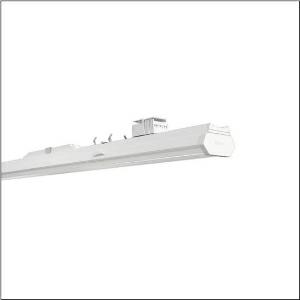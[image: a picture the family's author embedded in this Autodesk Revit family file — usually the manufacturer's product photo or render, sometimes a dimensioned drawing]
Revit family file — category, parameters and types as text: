
# Revit family: licross_11_protected_mo_51td12dn495g
name_source: partatom
category: Lighting Fixtures
units: mm (PartAtom-declared; Revit-internal decimal feet)

## family parameters
Cut with Voids When Loaded = No
Host = Face
Light Source = No
Part Type = Normal
Room Calculation Point = No
Round Connector Dimension = Use Diameter
Shared = No

## types (1)
- --- (1 x LED, 9980 lm, 57.1 W, 4000K)
    Apparent Load = 57 VA
    CIE Flux Codes = 73 92 98 99 100
    Color Rendering = 80
    Color Temperature = 4000K
    Default Elevation = 1800 mm
    Description = Licross 11 Protected MO, luminaire insert, of sheet steel, galvanised, coil coated, white, length: 1.500mm, width: 90mm, height: 101mm, LED rated luminous flux: 9.980lm, light colour: 840, SDCM (Standard Deviation of Colour Matching)MacAdam ≤ 2 SDCM (initial), control gear: DALI 2, with plug, 5-pole, with phase selection, mains connection: 220..240V, AC, 50/60Hz, rated input power: 57W, internal wiring halogen-free, primary optical cover: cover, of PMMA, light emission: direct distribution, primary light characteristic: symmetric, protection rating (complete): IP54, insulation class (complete): insulation class I (protective earthing), certification: CE, ENEC, VDE, UKCA, protection symbol: D if used in an environment with non-conductive dust loads with corresponding accessories, impact resistance: IK06, permissible ambient temperature for indoor applications: -25..+35°C, corresponds to IFS (International Featured Standards) requirements for safety and quality in the food industry, reducing of maximum allowable ambient temperature of 5°C with ceiling mounting, LABS conformity tested according to VDMA 24364:2018-05, The light source and the operating device comply with the requirements of the Ecodesign Regulation (EU) 2019/2020 and are replaceable in accordance with this regulation, packaging unit: 1 piece
    Height = 92 mm
    Lamp = 1 x LED
    Lamp Light Flux = 9980 lm
    Lamp Power = 57.1 W
    Lamp count = 1
    Length = 1500 mm
    Luminous efficacy = 175 lm/W
    Manufacturer = Siteco
    ModVariant = No
    Model = 51TD12DN495G
    Mounting Place = Ceiling
    Mounting Type = Pendant
    Number of Poles = 1
    OnlyDefault = Yes
    Power Factor = 1
    Product Name = Licross 11 Protected MO
    Product group = luminaire insert | ceiling pendant
    ProductGroupID = 901
    Protection Class = Protection class I
    Protection Degree = IP 54
    RLX_Detail_Level = 1
    RLX_Emergency_Light_Flux = 0 lm
    RLX_Emergency_Type = 0
    RLX_Emergency_Type_DB = No
    RlxData = <blob elided: 24633 chars, md5=99317bf8>
    Socket = socket
    Standby Power = 0 W
    System Light Flux = 9980 lm
    System Power = 57 W
    Type Comments = factory setting: luminous flux: 100 % | dim-lin: 254 | 378 mA
    Type Image = l_1256145.jpg
    URL = http://relux.com
    VarID = @adj_102725
    Voltage = 0 V
    Weight = 0.00 kg
    Width = 88 mm

## geometry (parser evidence)
native form markers: Blend x4, Sweep x11
no freeform markers — native parametric forms only
